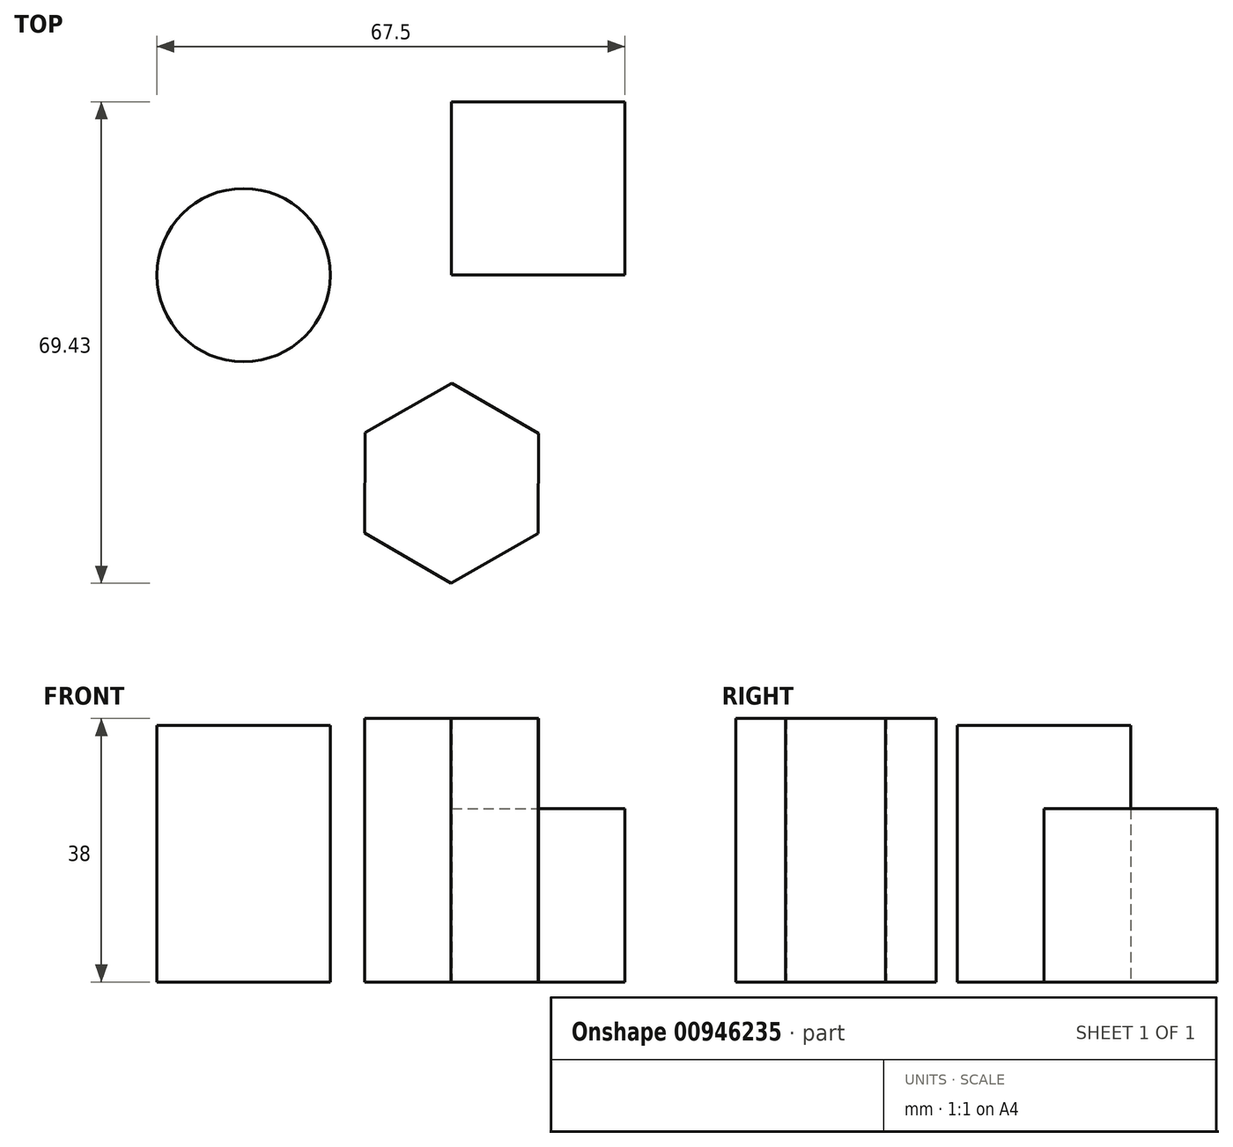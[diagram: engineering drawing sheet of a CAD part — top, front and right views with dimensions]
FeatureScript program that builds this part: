
annotation { "Feature Type Name" : "Feature", "Feature Type Description" : "" }
export const myFeature = defineFeature(function(context is Context, id is Id, definition is map)
    precondition{}
    {
        {
            var Q0;
            Q0=qCreatedBy(makeId("Top.planeOp"),FACE);
            var sketch = newSketch(context, id + "F0", { "sketchPlane" : qUnion([Q0])});
            skLineSegment(sketch, "E0.bottom", {"start": v(0, 0) * mm, "end": v(25, 0) * mm});
            skLineSegment(sketch, "E0.top", {"start": v(0, 25) * mm, "end": v(25, 25) * mm});
            skLineSegment(sketch, "E0.left", {"start": v(0, 0) * mm, "end": v(0, 25) * mm});
            skLineSegment(sketch, "E0.right", {"start": v(25, 0) * mm, "end": v(25, 25) * mm});
            skSolve(sketch);
        }
        {
            var Q0;
            Q0=makeQuery(id+"F0.imprint","IMPRINT",FACE,{"disambiguationData":[TD([[makeQuery(id+"F0.imprint","IMPRINT",EDGE,{"derivedFrom":sQuery(id+"F0.wireOp",EDGE,"E0.bottom")}),1.0]])]});
            extrude(context, id + "F1", {"entities" : qUnion([Q0]), "depth" : 25 * mm, "offsetDistance" : 25 * mm});
        }
        {
            var Q0;
            Q0=qCreatedBy(makeId("Top.planeOp"),FACE);
            var sketch = newSketch(context, id + "F2", { "sketchPlane" : qUnion([Q0])});
            skCircle(sketch, "E1", {"center": v(-30, 0) * mm, "radius": 12.5 * mm});
            skSolve(sketch);
        }
        {
            var Q0;
            Q0=makeQuery(id+"F2.imprint","IMPRINT",FACE,{"disambiguationData":[TD([[makeQuery(id+"F2.imprint","IMPRINT",EDGE,{"derivedFrom":sQuery(id+"F2.wireOp",EDGE,"E1")}),1.0]])]});
            extrude(context, id + "F3", {"entities" : qUnion([Q0]), "depth" : 37 * mm, "offsetDistance" : 25 * mm});
        }
        {
            var Q0;
            Q0=qCreatedBy(makeId("Top.planeOp"),FACE);
            var sketch = newSketch(context, id + "F4", { "sketchPlane" : qUnion([Q0])});
            skCircle(sketch, "E2.cCircle", {"center": v(0, -30) * mm, "radius": 12.5 * mm, "construction": true});
            skLineSegment(sketch, "E2.0", {"start": v(-12.47, -22.73) * mm, "end": v(0.06, -15.57) * mm});
            skLineSegment(sketch, "E2.1", {"start": v(0.06, -15.57) * mm, "end": v(12.53, -22.84) * mm});
            skLineSegment(sketch, "E2.2", {"start": v(12.53, -22.84) * mm, "end": v(12.47, -37.27) * mm});
            skLineSegment(sketch, "E2.3", {"start": v(12.47, -37.27) * mm, "end": v(-0.06, -44.43) * mm});
            skLineSegment(sketch, "E2.4", {"start": v(-0.06, -44.43) * mm, "end": v(-12.53, -37.16) * mm});
            skLineSegment(sketch, "E2.5", {"start": v(-12.53, -37.16) * mm, "end": v(-12.47, -22.73) * mm});
            skPoint(sketch, "E2.0.midPoint", {"position": v(-6.2, -19.15) * mm});
            skSolve(sketch);
        }
        {
            var Q0;
            Q0=makeQuery(id+"F4.imprint","IMPRINT",FACE,{"disambiguationData":[TD([[makeQuery(id+"F4.imprint","IMPRINT",EDGE,{"derivedFrom":sQuery(id+"F4.wireOp",EDGE,"E2.0")}),-1.0]])]});
            extrude(context, id + "F5", {"entities" : qUnion([Q0]), "depth" : 38 * mm, "offsetDistance" : 25 * mm});
        }
    });
